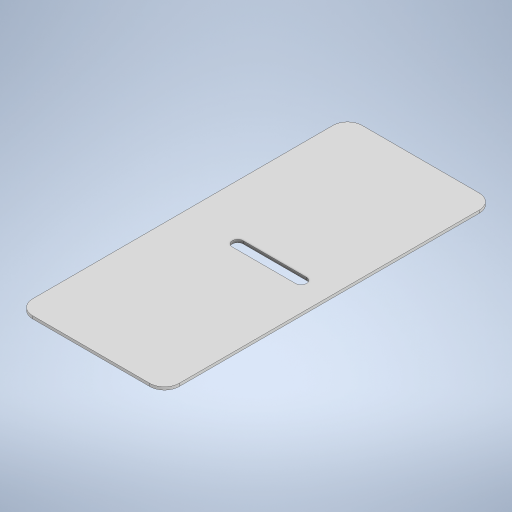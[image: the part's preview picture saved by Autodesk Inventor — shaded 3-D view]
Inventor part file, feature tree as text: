
AUTODESK INVENTOR PART (.ipt)
format: ipt  version: 2023 (Build 270158000, 158)  size: 229,376 bytes
history: native  units: in
note: dims shown in document units (in); Inventor stores cm internally (conversion verified against a paired STEP export)
features: extrude x2, sketch x2
ambient origin geometry x8: Origin, YZ Plane, XZ Plane, XY Plane, X Axis, Y Axis, Z Axis, Center Point
bodies: Solid1 (feature_tree)
feature tree (4):
  extrude  "Extrusion1"  Depth=0.7874in
  extrude  "Extrusion2"  Depth=0.015in TaperAngle=0.0deg
  sketch  "Sketch1"  dims[d0=1.7717in d1=0.7874in]
  sketch  "Sketch2"  dims[d2=0.0787in d3=0.015in d4=0.0in d5=0.0in d6=0.0in]
